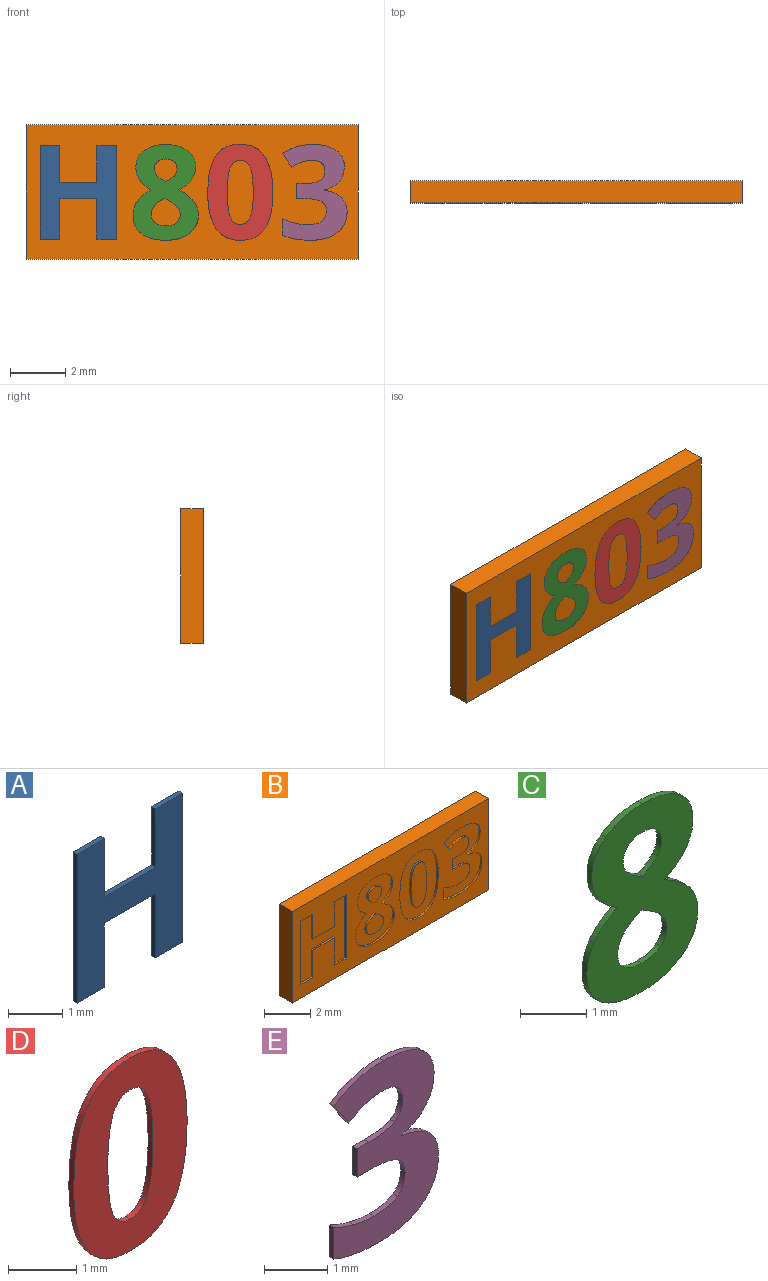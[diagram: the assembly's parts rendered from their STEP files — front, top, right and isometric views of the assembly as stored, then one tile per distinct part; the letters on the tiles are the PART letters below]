
ASSEMBLY  parts=5 mates=4
PART A: 14 faces, bbox 2.8x0.1x3.4 mm
  f0: plane 3.37x2.76mm, normal (0,-1,0), area 5.6mm2, adj f1,f2,f3,f4,f5,f6,f7,f8
  f1: plane 0.71x0.1mm, normal (0,0,1), area 0.1mm2, adj f0,f2,f10,f12
  f2: plane 1.32x0.1mm, normal (-1,0,0), area 0.1mm2, adj f0,f1,f3,f10
  f3: plane 1.33x0.1mm, normal (0,0,1), area 0.1mm2, adj f0,f2,f4,f10
  f4: plane 1.32x0.1mm, normal (1,0,0), area 0.1mm2, adj f0,f3,f5,f10
  f5: plane 0.72x0.1mm, normal (0,0,1), area 0.1mm2, adj f0,f4,f6,f10
  f6: plane 3.37x0.1mm, normal (-1,0,0), area 0.3mm2, adj f0,f5,f7,f10
  f7: plane 0.72x0.1mm, normal (0,0,-1), area 0.1mm2, adj f0,f6,f8,f10
  f8: plane 1.46x0.1mm, normal (1,0,0), area 0.1mm2, adj f0,f7,f9,f10
  f9: plane 1.33x0.1mm, normal (0,0,-1), area 0.1mm2, adj f0,f8,f10,f11
  f10: plane 3.37x2.76mm, normal (0,1,0), area 5.6mm2, adj f1,f2,f3,f4,f5,f6,f7,f8
  f11: plane 1.46x0.1mm, normal (-1,0,0), area 0.1mm2, adj f0,f9,f10,f13
  f12: plane 3.37x0.1mm, normal (1,0,0), area 0.3mm2, adj f0,f1,f10,f13
  f13: plane 0.71x0.1mm, normal (0,0,-1), area 0.1mm2, adj f0,f10,f11,f12
PART B: 99 faces, bbox 12x0.8x4.9 mm
  f0: plane 12x4.85mm, normal (0,-1,0), area 35mm2, adj f1,f2,f3,f4,f6,f7,f8,f9
  f1: plane 12x0.8mm, normal (0,0,-1), area 9.6mm2, adj f0,f2,f4,f5
  f2: plane 4.85x0.8mm, normal (1,0,0), area 3.9mm2, adj f0,f1,f3,f5
  f3: plane 12x0.8mm, normal (0,0,1), area 9.6mm2, adj f0,f2,f4,f5
  f4: plane 4.85x0.8mm, normal (-1,0,0), area 3.9mm2, adj f0,f1,f3,f5
  f5: plane 12x4.85mm, normal (0,1,0), area 58.2mm2, adj f1,f2,f3,f4
  f6: extruded ~0.78x0.22mm, area 0.1mm2, adj f0,f7,f36,f37
  f7: extruded ~0.59x0.3mm, area 0.1mm2, adj f0,f6,f8,f37
  f8: extruded ~0.45x0.13mm, area 0mm2, adj f0,f7,f9,f37
  f9: extruded ~0.42x0.39mm, area 0.1mm2, adj f0,f8,f10,f37
  f10: extruded ~0.49x0.39mm, area 0.1mm2, adj f0,f9,f11,f37
  f11: extruded ~0.51x0.15mm, area 0.1mm2, adj f0,f10,f12,f37
  f12: extruded ~0.67x0.32mm, area 0.1mm2, adj f0,f11,f13,f37
  f13: extruded ~0.87x0.24mm, area 0.1mm2, adj f0,f12,f14,f37
  f14: extruded ~0.86x0.25mm, area 0.1mm2, adj f0,f13,f15,f37
  f15: extruded ~0.67x0.33mm, area 0.1mm2, adj f0,f14,f16,f37
  f16: extruded ~0.48x0.17mm, area 0.1mm2, adj f0,f15,f17,f37
  f17: extruded ~0.54x0.42mm, area 0.1mm2, adj f0,f16,f18,f37
  f18: extruded ~0.46x0.36mm, area 0.1mm2, adj f0,f17,f19,f37
  f19: extruded ~0.46x0.14mm, area 0mm2, adj f0,f18,f20,f37
  f20: extruded ~0.59x0.3mm, area 0.1mm2, adj f0,f19,f36,f37
  f21: extruded ~0.57x0.49mm, area 0.1mm2, adj f22,f34,f37,f39
  f22: extruded ~0.42x0.29mm, area 0.1mm2, adj f21,f23,f37,f39
  f23: extruded ~0.29x0.13mm, area 0mm2, adj f22,f24,f37,f39
  f24: extruded ~0.3x0.13mm, area 0mm2, adj f23,f25,f37,f39
  f25: extruded ~0.4x0.11mm, area 0mm2, adj f24,f26,f37,f39
  f26: extruded ~0.38x0.11mm, area 0mm2, adj f25,f34,f37,f39
  f27: extruded ~0.3x0.1mm, area 0mm2, adj f28,f35,f37,f38
  f28: extruded ~0.25x0.12mm, area 0mm2, adj f27,f29,f37,f38
  f29: extruded ~0.26x0.1mm, area 0mm2, adj f28,f30,f37,f38
  f30: extruded ~0.32x0.22mm, area 0mm2, adj f29,f31,f37,f38
  f31: extruded ~0.32x0.22mm, area 0mm2, adj f30,f32,f37,f38
  f32: extruded ~0.25x0.1mm, area 0mm2, adj f31,f33,f37,f38
  f33: extruded ~0.25x0.11mm, area 0mm2, adj f32,f35,f37,f38
  f34: extruded ~0.31x0.14mm, area 0mm2, adj f21,f26,f37,f39
  f35: extruded ~0.29x0.1mm, area 0mm2, adj f27,f33,f37,f38
  f36: extruded ~0.78x0.22mm, area 0.1mm2, adj f0,f6,f20,f37
  f37: plane 3.46x2.37mm, normal (0,-1,0), area 5.2mm2, adj f6,f7,f8,f9,f10,f11,f12,f13
  f38: plane 0.82x0.82mm, normal (0,-1,0), area 0.5mm2, adj f27,f28,f29,f30,f31,f32,f33,f35
  f39: plane 1.04x0.99mm, normal (0,-1,0), area 0.8mm2, adj f21,f22,f23,f24,f25,f26,f34
  f40: extruded ~1.3x0.3mm, area 0.1mm2, adj f0,f41,f55,f56
  f41: extruded ~0.88x0.44mm, area 0.1mm2, adj f0,f40,f42,f56
  f42: extruded ~0.89x0.42mm, area 0.1mm2, adj f0,f41,f43,f56
  f43: extruded ~1.32x0.29mm, area 0.1mm2, adj f0,f42,f44,f56
  f44: extruded ~1.29x0.3mm, area 0.1mm2, adj f0,f43,f45,f56
  f45: extruded ~0.88x0.44mm, area 0.1mm2, adj f0,f44,f46,f56
  f46: extruded ~0.89x0.42mm, area 0.1mm2, adj f0,f45,f55,f56
  f47: extruded ~0.89x0.11mm, area 0.1mm2, adj f48,f54,f56,f57
  f48: extruded ~0.36x0.27mm, area 0mm2, adj f47,f49,f56,f57
  f49: extruded ~0.36x0.27mm, area 0mm2, adj f48,f50,f56,f57
  f50: extruded ~0.89x0.11mm, area 0.1mm2, adj f49,f51,f56,f57
  f51: extruded ~0.89x0.11mm, area 0.1mm2, adj f50,f52,f56,f57
  f52: extruded ~0.36x0.27mm, area 0mm2, adj f51,f53,f56,f57
  f53: extruded ~0.36x0.27mm, area 0mm2, adj f52,f54,f56,f57
  f54: extruded ~0.89x0.11mm, area 0.1mm2, adj f47,f53,f56,f57
  f55: extruded ~1.31x0.29mm, area 0.1mm2, adj f0,f40,f46,f56
  f56: plane 3.47x2.36mm, normal (0,-1,0), area 5mm2, adj f40,f41,f42,f43,f44,f45,f46,f47
  f57: plane 2.32x0.94mm, normal (0,-1,0), area 1.8mm2, adj f47,f48,f49,f50,f51,f52,f53,f54
  f58: extruded ~0.59x0.3mm, area 0.1mm2, adj f0,f59,f84,f85
  f59: extruded ~0.83x0.21mm, area 0.1mm2, adj f0,f58,f60,f85
  f60: extruded ~1.1x0.33mm, area 0.1mm2, adj f0,f59,f61,f85
  f61: plane 0.49x0.33mm, normal (0.83,0,0.56), area 0.1mm2, adj f0,f60,f62,f85
  f62: extruded ~0.38x0.19mm, area 0mm2, adj f0,f61,f63,f85
  f63: extruded ~0.34x0.1mm, area 0mm2, adj f0,f62,f64,f85
  f64: extruded ~0.48x0.38mm, area 0.1mm2, adj f0,f63,f65,f85
  f65: extruded ~0.35x0.18mm, area 0mm2, adj f0,f64,f66,f85
  f66: extruded ~0.57x0.1mm, area 0.1mm2, adj f0,f65,f67,f85
  f67: plane 0.26x0.1mm, normal (0,0,-1), area 0mm2, adj f0,f66,f68,f85
  f68: plane 0.55x0.1mm, normal (1,0,0), area 0.1mm2, adj f0,f67,f69,f85
  f69: plane 0.26x0.1mm, normal (0,0,1), area 0mm2, adj f0,f68,f70,f85
  f70: extruded ~0.62x0.1mm, area 0.1mm2, adj f0,f69,f71,f85
  f71: extruded ~0.34x0.19mm, area 0mm2, adj f0,f70,f72,f85
  f72: extruded ~0.39x0.17mm, area 0mm2, adj f0,f71,f73,f85
  f73: extruded ~0.52x0.12mm, area 0.1mm2, adj f0,f72,f74,f85
  f74: extruded ~0.47x0.1mm, area 0mm2, adj f0,f73,f75,f85
  f75: extruded ~0.43x0.16mm, area 0mm2, adj f0,f74,f76,f85
  f76: plane 0.61x0.1mm, normal (1,0,0), area 0.1mm2, adj f0,f75,f77,f85
  f77: extruded ~0.97x0.18mm, area 0.1mm2, adj f0,f76,f78,f85
  f78: extruded ~1.01x0.27mm, area 0.1mm2, adj f0,f77,f79,f85
  f79: extruded ~0.76x0.35mm, area 0.1mm2, adj f0,f78,f80,f85
  f80: extruded ~0.53x0.21mm, area 0.1mm2, adj f0,f79,f81,f85
  f81: extruded ~0.62x0.25mm, area 0.1mm2, adj f0,f80,f82,f85
  f82: plane 0.1x0.01mm, normal (-1,0,0), area 0mm2, adj f0,f81,f83,f85
  f83: extruded ~0.54x0.3mm, area 0.1mm2, adj f0,f82,f84,f85
  f84: extruded ~0.54x0.19mm, area 0.1mm2, adj f0,f58,f83,f85
  f85: plane 3.47x2.33mm, normal (0,-1,0), area 4.3mm2, adj f58,f59,f60,f61,f62,f63,f64,f65
  f86: plane 3.37x0.1mm, normal (-1,0,0), area 0.3mm2, adj f0,f87,f97,f98
  f87: plane 0.71x0.1mm, normal (0,0,-1), area 0.1mm2, adj f0,f86,f88,f98
  f88: plane 1.32x0.1mm, normal (1,0,0), area 0.1mm2, adj f0,f87,f89,f98
  f89: plane 1.33x0.1mm, normal (0,0,-1), area 0.1mm2, adj f0,f88,f90,f98
  f90: plane 1.32x0.1mm, normal (-1,0,0), area 0.1mm2, adj f0,f89,f91,f98
  f91: plane 0.72x0.1mm, normal (0,0,-1), area 0.1mm2, adj f0,f90,f92,f98
  f92: plane 3.37x0.1mm, normal (1,0,0), area 0.3mm2, adj f0,f91,f93,f98
  f93: plane 0.72x0.1mm, normal (0,0,1), area 0.1mm2, adj f0,f92,f94,f98
  f94: plane 1.46x0.1mm, normal (-1,0,0), area 0.1mm2, adj f0,f93,f95,f98
  f95: plane 1.33x0.1mm, normal (0,0,1), area 0.1mm2, adj f0,f94,f96,f98
  f96: plane 1.46x0.1mm, normal (1,0,0), area 0.1mm2, adj f0,f95,f97,f98
  f97: plane 0.71x0.1mm, normal (0,0,1), area 0.1mm2, adj f0,f86,f96,f98
  f98: plane 3.37x2.76mm, normal (0,-1,0), area 5.6mm2, adj f86,f87,f88,f89,f90,f91,f92,f93
PART C: 33 faces, bbox 2.4x0.1x3.5 mm
  f0: plane 3.46x2.37mm, normal (0,-1,0), area 5.2mm2, adj f1,f2,f3,f4,f5,f6,f7,f8
  f1: extruded ~0.59x0.3mm, area 0.1mm2, adj f0,f2,f23,f25
  f2: extruded ~0.45x0.13mm, area 0mm2, adj f0,f1,f3,f23
  f3: extruded ~0.42x0.39mm, area 0.1mm2, adj f0,f2,f4,f23
  f4: extruded ~0.49x0.39mm, area 0.1mm2, adj f0,f3,f5,f23
  f5: extruded ~0.51x0.15mm, area 0.1mm2, adj f0,f4,f6,f23
  f6: extruded ~0.67x0.32mm, area 0.1mm2, adj f0,f5,f7,f23
  f7: extruded ~0.87x0.24mm, area 0.1mm2, adj f0,f6,f8,f23
  f8: extruded ~0.86x0.25mm, area 0.1mm2, adj f0,f7,f9,f23
  f9: extruded ~0.67x0.33mm, area 0.1mm2, adj f0,f8,f10,f23
  f10: extruded ~0.48x0.17mm, area 0.1mm2, adj f0,f9,f11,f23
  f11: extruded ~0.54x0.42mm, area 0.1mm2, adj f0,f10,f12,f23
  f12: extruded ~0.46x0.36mm, area 0.1mm2, adj f0,f11,f13,f23
  f13: extruded ~0.46x0.14mm, area 0mm2, adj f0,f12,f23,f24
  f14: extruded ~0.42x0.29mm, area 0.1mm2, adj f0,f15,f23,f31
  f15: extruded ~0.29x0.13mm, area 0mm2, adj f0,f14,f16,f23
  f16: extruded ~0.3x0.13mm, area 0mm2, adj f0,f15,f17,f23
  f17: extruded ~0.4x0.11mm, area 0mm2, adj f0,f16,f23,f30
  f18: extruded ~0.25x0.12mm, area 0mm2, adj f0,f19,f23,f28
  f19: extruded ~0.26x0.1mm, area 0mm2, adj f0,f18,f20,f23
  f20: extruded ~0.32x0.22mm, area 0mm2, adj f0,f19,f21,f23
  f21: extruded ~0.32x0.22mm, area 0mm2, adj f0,f20,f22,f23
  f22: extruded ~0.25x0.1mm, area 0mm2, adj f0,f21,f23,f27
  f23: plane 3.46x2.37mm, normal (0,1,0), area 5.2mm2, adj f1,f2,f3,f4,f5,f6,f7,f8
  f24: extruded ~0.59x0.3mm, area 0.1mm2, adj f0,f13,f23,f26
  f25: extruded ~0.78x0.22mm, area 0.1mm2, adj f0,f1,f23,f26
  f26: extruded ~0.78x0.22mm, area 0.1mm2, adj f0,f23,f24,f25
  f27: extruded ~0.25x0.11mm, area 0mm2, adj f0,f22,f23,f29
  f28: extruded ~0.3x0.1mm, area 0mm2, adj f0,f18,f23,f29
  f29: extruded ~0.29x0.1mm, area 0mm2, adj f0,f23,f27,f28
  f30: extruded ~0.38x0.11mm, area 0mm2, adj f0,f17,f23,f32
  f31: extruded ~0.57x0.49mm, area 0.1mm2, adj f0,f14,f23,f32
  f32: extruded ~0.31x0.14mm, area 0mm2, adj f0,f23,f30,f31
PART D: 18 faces, bbox 2.4x0.1x3.5 mm
  f0: plane 3.47x2.36mm, normal (0,-1,0), area 5mm2, adj f1,f2,f3,f4,f5,f6,f7,f8
  f1: extruded ~0.88x0.44mm, area 0.1mm2, adj f0,f2,f11,f13
  f2: extruded ~0.89x0.42mm, area 0.1mm2, adj f0,f1,f3,f11
  f3: extruded ~1.32x0.29mm, area 0.1mm2, adj f0,f2,f4,f11
  f4: extruded ~1.29x0.3mm, area 0.1mm2, adj f0,f3,f5,f11
  f5: extruded ~0.88x0.44mm, area 0.1mm2, adj f0,f4,f11,f12
  f6: extruded ~0.36x0.27mm, area 0mm2, adj f0,f7,f11,f16
  f7: extruded ~0.36x0.27mm, area 0mm2, adj f0,f6,f8,f11
  f8: extruded ~0.89x0.11mm, area 0.1mm2, adj f0,f7,f9,f11
  f9: extruded ~0.89x0.11mm, area 0.1mm2, adj f0,f8,f10,f11
  f10: extruded ~0.36x0.27mm, area 0mm2, adj f0,f9,f11,f15
  f11: plane 3.47x2.36mm, normal (0,1,0), area 5mm2, adj f1,f2,f3,f4,f5,f6,f7,f8
  f12: extruded ~0.89x0.42mm, area 0.1mm2, adj f0,f5,f11,f14
  f13: extruded ~1.3x0.3mm, area 0.1mm2, adj f0,f1,f11,f14
  f14: extruded ~1.31x0.29mm, area 0.1mm2, adj f0,f11,f12,f13
  f15: extruded ~0.36x0.27mm, area 0mm2, adj f0,f10,f11,f17
  f16: extruded ~0.89x0.11mm, area 0.1mm2, adj f0,f6,f11,f17
  f17: extruded ~0.89x0.11mm, area 0.1mm2, adj f0,f11,f15,f16
PART E: 29 faces, bbox 2.3x0.1x3.5 mm
  f0: plane 3.47x2.33mm, normal (0,-1,0), area 4.3mm2, adj f1,f2,f3,f4,f5,f6,f7,f8
  f1: extruded ~0.83x0.21mm, area 0.1mm2, adj f0,f2,f25,f27
  f2: extruded ~1.1x0.33mm, area 0.1mm2, adj f0,f1,f3,f25
  f3: plane 0.49x0.33mm, normal (-0.83,0,-0.56), area 0.1mm2, adj f0,f2,f4,f25
  f4: extruded ~0.38x0.19mm, area 0mm2, adj f0,f3,f5,f25
  f5: extruded ~0.34x0.1mm, area 0mm2, adj f0,f4,f6,f25
  f6: extruded ~0.48x0.38mm, area 0.1mm2, adj f0,f5,f7,f25
  f7: extruded ~0.35x0.18mm, area 0mm2, adj f0,f6,f8,f25
  f8: extruded ~0.57x0.1mm, area 0.1mm2, adj f0,f7,f9,f25
  f9: plane 0.26x0.1mm, normal (0,0,1), area 0mm2, adj f0,f8,f10,f25
  f10: plane 0.55x0.1mm, normal (-1,0,0), area 0.1mm2, adj f0,f9,f11,f25
  f11: plane 0.26x0.1mm, normal (0,0,-1), area 0mm2, adj f0,f10,f12,f25
  f12: extruded ~0.62x0.1mm, area 0.1mm2, adj f0,f11,f13,f25
  f13: extruded ~0.34x0.19mm, area 0mm2, adj f0,f12,f14,f25
  f14: extruded ~0.39x0.17mm, area 0mm2, adj f0,f13,f15,f25
  f15: extruded ~0.52x0.12mm, area 0.1mm2, adj f0,f14,f16,f25
  f16: extruded ~0.47x0.1mm, area 0mm2, adj f0,f15,f17,f25
  f17: extruded ~0.43x0.16mm, area 0mm2, adj f0,f16,f18,f25
  f18: plane 0.61x0.1mm, normal (-1,0,0), area 0.1mm2, adj f0,f17,f19,f25
  f19: extruded ~0.97x0.18mm, area 0.1mm2, adj f0,f18,f20,f25
  f20: extruded ~1.01x0.27mm, area 0.1mm2, adj f0,f19,f21,f25
  f21: extruded ~0.76x0.35mm, area 0.1mm2, adj f0,f20,f22,f25
  f22: extruded ~0.53x0.21mm, area 0.1mm2, adj f0,f21,f23,f25
  f23: extruded ~0.62x0.25mm, area 0.1mm2, adj f0,f22,f24,f25
  f24: plane 0.1x0.01mm, normal (1,0,0), area 0mm2, adj f0,f23,f25,f26
  f25: plane 3.47x2.33mm, normal (0,1,0), area 4.3mm2, adj f1,f2,f3,f4,f5,f6,f7,f8
  f26: extruded ~0.54x0.3mm, area 0.1mm2, adj f0,f24,f25,f28
  f27: extruded ~0.59x0.3mm, area 0.1mm2, adj f0,f1,f25,f28
  f28: extruded ~0.54x0.19mm, area 0.1mm2, adj f0,f25,f26,f27
PLACE A t=(0.19,0.64,0.19)mm
PLACE B t=(0.19,0.64,0.19)mm
PLACE C t=(-2.25,0.64,0.19)mm
PLACE D t=(-0.91,0.64,0.19)mm
PLACE E t=(3.13,0.64,0.19)mm
MATE fastened D.f0 <-> B.f57  axis (0,-1,0) through (1.94,-0.16,-0.98)mm
MATE fastened C.f0 <-> B.f0  axis (0,-1,0) through (-0.75,-0.16,-1.56)mm
MATE fastened E.f0 <-> B.f0  axis (0,-1,0) through (3.47,-0.16,-1.38)mm
MATE fastened A.f0 <-> B.f0  axis (0,-1,0) through (-5.29,-0.16,-1.51)mm
